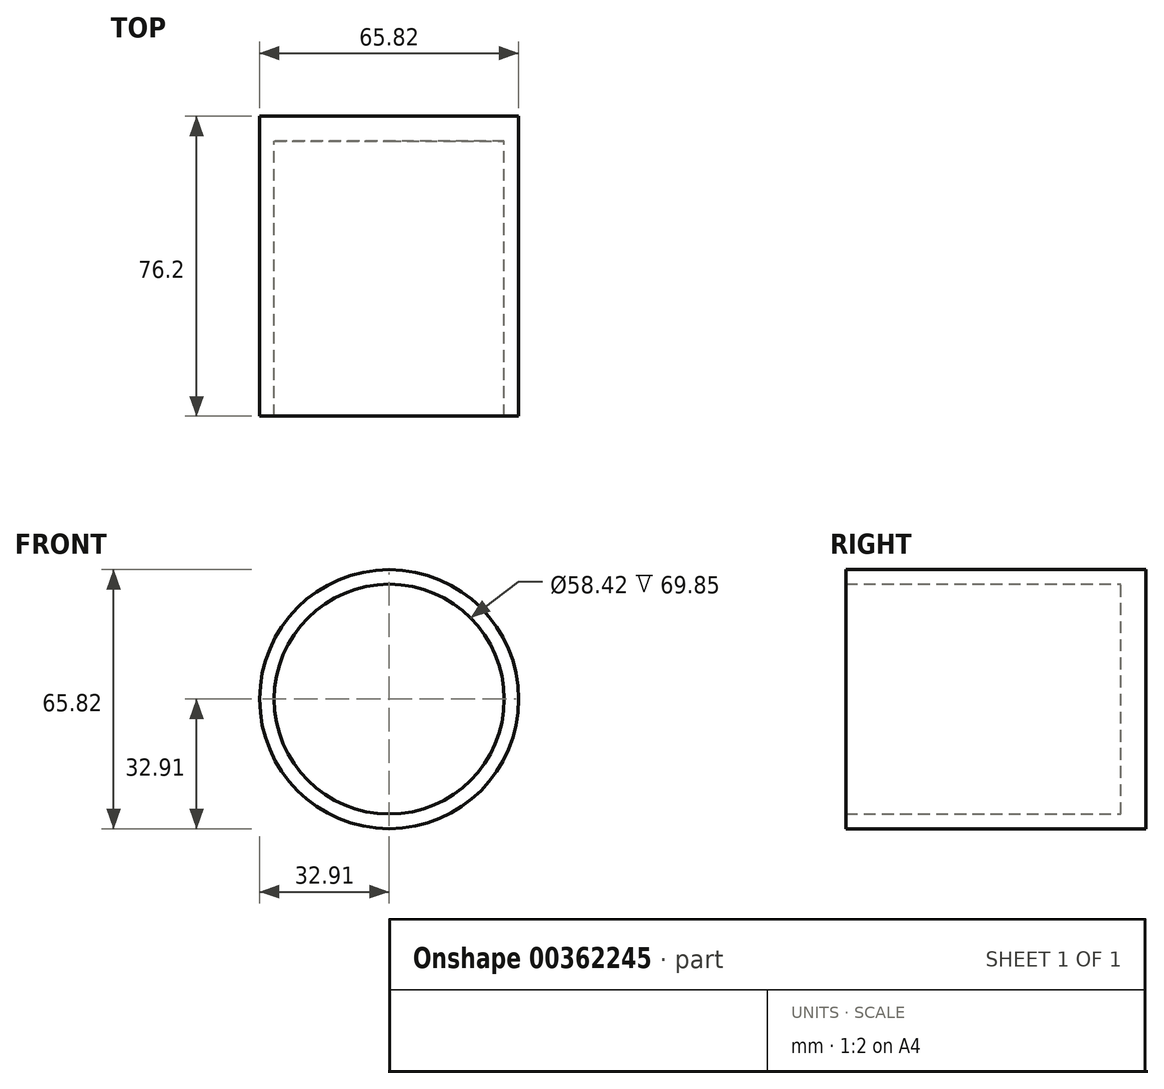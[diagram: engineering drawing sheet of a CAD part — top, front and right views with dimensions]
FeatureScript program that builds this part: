
annotation { "Feature Type Name" : "Feature", "Feature Type Description" : "" }
export const myFeature = defineFeature(function(context is Context, id is Id, definition is map)
    precondition{}
    {
        {
            var Q0;
            Q0=qCreatedBy(makeId("Front.planeOp"),FACE);
            var sketch = newSketch(context, id + "F0", { "sketchPlane" : qUnion([Q0])});
            skCircle(sketch, "E0", {"center": v(0, 0) * mm, "radius": 32.9 * mm});
            skSolve(sketch);
        }
        {
            var Q0;
            Q0=qCreatedBy(makeId("Front.planeOp"),FACE);
            var sketch = newSketch(context, id + "F1", { "sketchPlane" : qUnion([Q0])});
            skCircle(sketch, "E1", {"center": v(0, 0) * mm, "radius": 29.33 * mm});
            skSolve(sketch);
        }
        {
            var Q0;
            Q0=makeQuery(id+"F0.imprint","IMPRINT",FACE,{"disambiguationData":[TD([[makeQuery(id+"F0.imprint","IMPRINT",EDGE,{"derivedFrom":sQuery(id+"F0.wireOp",EDGE,"E0")}),1.0]])]});
            extrude(context, id + "F2", {"entities" : qUnion([Q0]), "depth" : 76.2 * mm});
        }
        {
            var Q0;
            Q0=sQuery(id+"F1.wireOp",VERTEX,"E1.center");
            var Q1;
            Q1=makeQuery(id+"F2.opExtrude","SWEPT_BODY",BODY,{"disambiguationData":[OSD([sQuery(id+"F0.wireOp",EDGE,"E0")])]});
            hole(context, id + "F3", {"style" : HoleStyle.SIMPLE, "endStyle" : HoleEndStyle.THROUGH, "oppositeDirection" : true, "holeDiameter" : 58.42 * mm, "isTappedThrough" : true, "tappedDepth" : 12.7 * mm, "tapClearance" : 3, "locations" : qUnion([Q0]), "scope" : qUnion([Q1])});
        }
        {
            var Q0;
            Q0=qCreatedBy(makeId("Front.planeOp"),FACE);
            var sketch = newSketch(context, id + "F4", { "sketchPlane" : qUnion([Q0])});
            skCircle(sketch, "E2", {"center": v(0, 0) * mm, "radius": 30.28 * mm});
            skSolve(sketch);
        }
        {
            var Q0;
            Q0=makeQuery(id+"F4.imprint","IMPRINT",FACE,{"disambiguationData":[TD([[makeQuery(id+"F4.imprint","IMPRINT",EDGE,{"derivedFrom":sQuery(id+"F4.wireOp",EDGE,"E2")}),1.0]])]});
            extrude(context, id + "F5", {"entities" : qUnion([Q0]), "operationType" : NewBodyOperationType.ADD, "depth" : 6.35 * mm});
        }
    });
